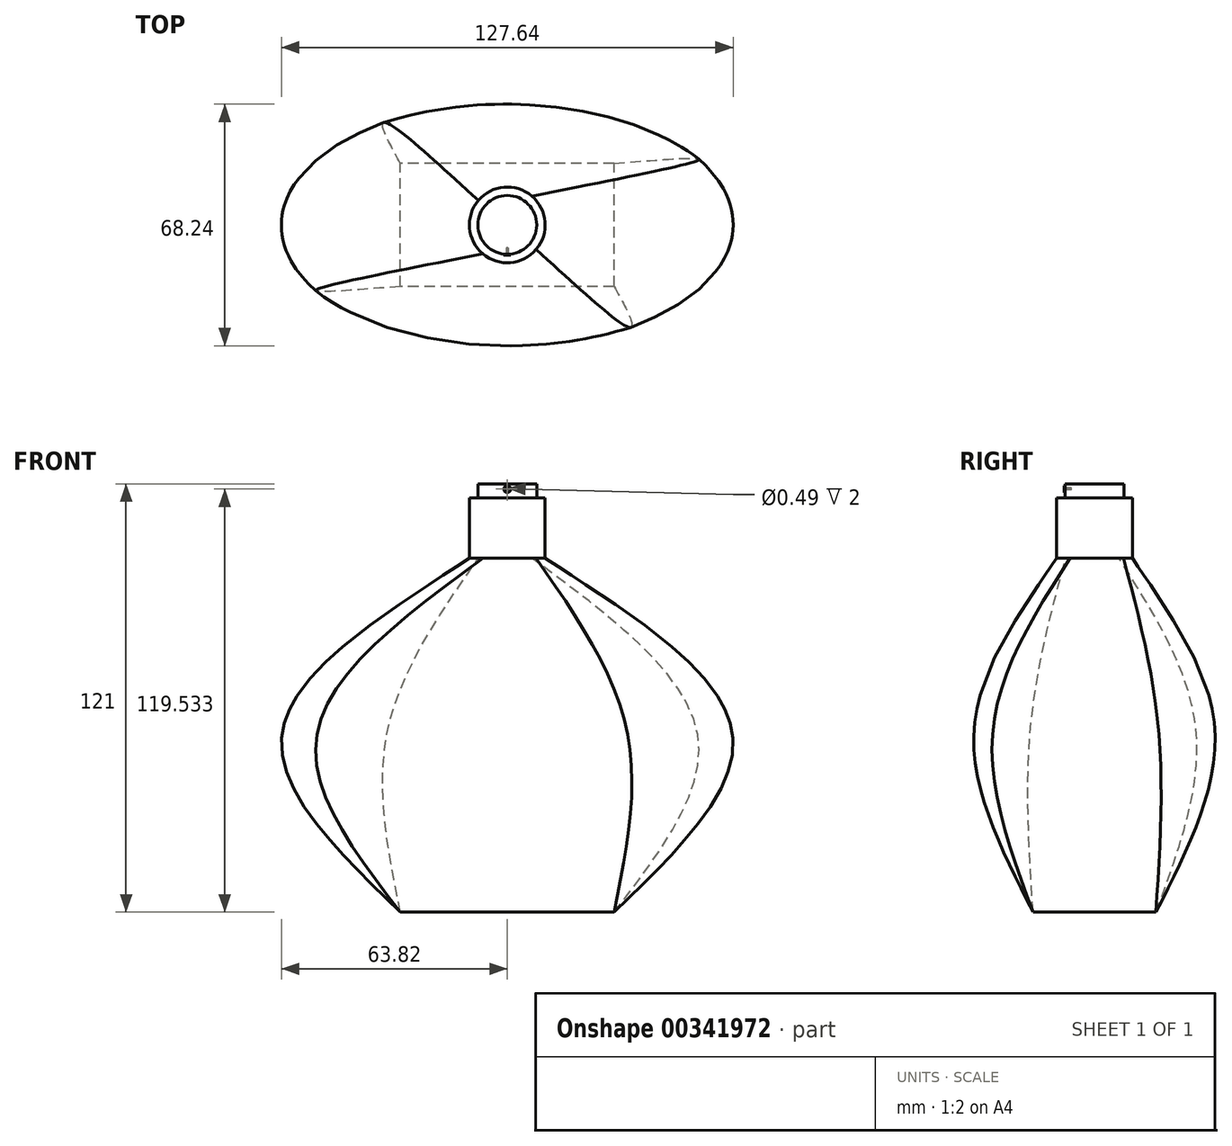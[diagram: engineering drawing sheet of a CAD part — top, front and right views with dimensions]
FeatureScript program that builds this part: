
annotation { "Feature Type Name" : "Feature", "Feature Type Description" : "" }
export const myFeature = defineFeature(function(context is Context, id is Id, definition is map)
    precondition{}
    {
        {
            var Q0;
            Q0=qCreatedBy(makeId("Top.planeOp"),FACE);
            cPlane(context, id + "F0", {"entities" : qUnion([Q0]), "cplaneType" : CPlaneType.OFFSET, "offset" : 50 * mm, "width" : 150 * mm, "height" : 150 * mm});
        }
        {
            var Q0;
            Q0=qCreatedBy(makeId("Top.planeOp"),FACE);
            var sketch = newSketch(context, id + "F1", { "sketchPlane" : qUnion([Q0])});
            skLineSegment(sketch, "E0.bottom", {"start": v(30.17, -17.37) * mm, "end": v(-30.17, -17.37) * mm});
            skLineSegment(sketch, "E0.top", {"start": v(30.17, 17.37) * mm, "end": v(-30.17, 17.37) * mm});
            skLineSegment(sketch, "E0.left", {"start": v(30.17, -17.37) * mm, "end": v(30.17, 17.37) * mm});
            skLineSegment(sketch, "E0.right", {"start": v(-30.17, -17.37) * mm, "end": v(-30.17, 17.37) * mm});
            skPoint(sketch, "E0.middle", {"position": v(0, 0) * mm});
            skSolve(sketch);
        }
        {
            var Q0;
            Q0=qCreatedBy(id+"F0.planeOp",FACE);
            var sketch = newSketch(context, id + "F2", { "sketchPlane" : qUnion([Q0])});
            skEllipse(sketch, "E1", {"center": v(0, 0) * mm, "majorRadius": 63.69 * mm, "minorRadius": 34.1 * mm, "majorAxis": v(1, 0)});
            skSolve(sketch);
        }
        {
            var Q0;
            Q0=qCreatedBy(id+"F0.planeOp",FACE);
            cPlane(context, id + "F3", {"entities" : qUnion([Q0]), "cplaneType" : CPlaneType.OFFSET, "offset" : 50 * mm, "width" : 150 * mm, "height" : 150 * mm});
        }
        {
            var Q0;
            Q0=qCreatedBy(id+"F3.planeOp",FACE);
            var sketch = newSketch(context, id + "F4", { "sketchPlane" : qUnion([Q0])});
            skCircle(sketch, "E2", {"center": v(0, 0) * mm, "radius": 10.7 * mm});
            skSolve(sketch);
        }
        {
            var Q0;
            Q0=makeQuery(id+"F1.imprint","IMPRINT",FACE,{"disambiguationData":[TD([[makeQuery(id+"F1.imprint","IMPRINT",EDGE,{"derivedFrom":sQuery(id+"F1.wireOp",EDGE,"E0.bottom")}),-1.0]])]});
            var Q1;
            Q1=makeQuery(id+"F2.imprint","IMPRINT",FACE,{"disambiguationData":[TD([[makeQuery(id+"F2.imprint","IMPRINT",EDGE,{"derivedFrom":sQuery(id+"F2.wireOp",EDGE,"E1")}),1.0]])]});
            var Q2;
            Q2=makeQuery(id+"F4.imprint","IMPRINT",FACE,{"disambiguationData":[TD([[makeQuery(id+"F4.imprint","IMPRINT",EDGE,{"derivedFrom":sQuery(id+"F4.wireOp",EDGE,"E2")}),1.0]])]});
            loft(context, id + "F5", {"sheetProfilesArray" : [{ "sheetProfileEntities" : qUnion([Q0]) }, { "sheetProfileEntities" : qUnion([Q1]) }, { "sheetProfileEntities" : qUnion([Q2]) }]});
        }
        {
            var Q0;
            Q0=makeQuery(id+"F5.opLoft","CAP_FACE",FACE,{"disambiguationData":[OSD([makeQuery(id+"F4.imprint","IMPRINT",FACE,{"disambiguationData":[TD([[makeQuery(id+"F4.imprint","IMPRINT",EDGE,{"derivedFrom":sQuery(id+"F4.wireOp",EDGE,"E2")}),1.0]])]})])],"isStart":true});
            extrude(context, id + "F6", {"entities" : qUnion([Q0]), "operationType" : NewBodyOperationType.ADD, "depth" : 17 * mm});
        }
        {
            var Q0;
            Q0=makeQuery(id+"F6.opExtrude","CAP_FACE",FACE,{"disambiguationData":[OSD([makeQuery(id+"F4.imprint","IMPRINT",FACE,{"disambiguationData":[TD([[makeQuery(id+"F4.imprint","IMPRINT",EDGE,{"derivedFrom":sQuery(id+"F4.wireOp",EDGE,"E2")}),1.0]])]})])],"isStart":false});
            var sketch = newSketch(context, id + "F7", { "sketchPlane" : qUnion([Q0])});
            skCircle(sketch, "E3", {"center": v(0, 0) * mm, "radius": 8.32 * mm});
            skSolve(sketch);
        }
        {
            var Q0;
            Q0=makeQuery(id+"F7.imprint","IMPRINT",FACE,{"disambiguationData":[TD([[makeQuery(id+"F7.imprint","IMPRINT",EDGE,{"derivedFrom":sQuery(id+"F7.wireOp",EDGE,"E3")}),1.0]])]});
            extrude(context, id + "F8", {"entities" : qUnion([Q0]), "operationType" : NewBodyOperationType.ADD, "depth" : 4 * mm});
        }
        {
            var Q0;
            Q0=qCreatedBy(makeId("Front.planeOp"),FACE);
            var sketch = newSketch(context, id + "F9", { "sketchPlane" : qUnion([Q0])});
            skCircle(sketch, "E4", {"center": v(0, 119.5) * mm, "radius": 0.97 * mm});
            skSolve(sketch);
        }
        {
            var Q0;
            Q0 = qSketchRegion(id + "F9", true);
            extrude(context, id + "F10", {"entities" : qUnion([Q0]), "operationType" : NewBodyOperationType.ADD, "depth" : 8.5 * mm});
        }
        {
            var Q0;
            Q0=makeQuery(id+"F10.opExtrude","CAP_FACE",FACE,{"disambiguationData":[OSD([sQuery(id+"F9.wireOp",EDGE,"E4")])],"isStart":false});
            var sketch = newSketch(context, id + "F11", { "sketchPlane" : qUnion([Q0])});
            skSolve(sketch);
        }
        {
            var Q0;
            Q0=makeQuery(id+"F11.imprint","IMPRINT",FACE,{"disambiguationData":[TD([[makeQuery(id+"F11.imprint","IMPRINT",EDGE,{"derivedFrom":makeQuery(id+"F10.opExtrude","CAP_EDGE",EDGE,{"disambiguationData":[OSD([sQuery(id+"F9.wireOp",EDGE,"E4")])],"isStart":false})}),1.0]])]});
            var sketch = newSketch(context, id + "F12", { "sketchPlane" : qUnion([Q0])});
            skCircle(sketch, "E5", {"center": v(0, 119.53) * mm, "radius": 0.25 * mm});
            skSolve(sketch);
        }
        {
            var Q0;
            Q0 = qSketchRegion(id + "F12", true);
            extrude(context, id + "F13", {"entities" : qUnion([Q0]), "operationType" : NewBodyOperationType.REMOVE, "oppositeDirection" : true, "depth" : 2 * mm});
        }
        {
            var Q0;
            Q0=qCreatedBy(makeId("Front.planeOp"),FACE);
            var sketch = newSketch(context, id + "F14", { "sketchPlane" : qUnion([Q0])});
            skCircle(sketch, "E6", {"center": v(0, 119.52) * mm, "radius": 0.07 * mm});
            skSolve(sketch);
        }
        {
            var Q0;
            Q0 = qSketchRegion(id + "F14", true);
            extrude(context, id + "F15", {"entities" : qUnion([Q0]), "operationType" : NewBodyOperationType.ADD, "depth" : 8.5 * mm});
        }
    });
